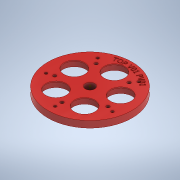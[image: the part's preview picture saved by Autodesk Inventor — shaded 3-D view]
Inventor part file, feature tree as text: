
AUTODESK INVENTOR PART (.ipt)
format: ipt  version: 2022.2 (Build 262287000, 287)  size: 698,880 bytes
history: native  units: in
note: dims shown in document units (in); Inventor stores cm internally (conversion verified against a paired STEP export)
features: sketch x8, extrude x5, hole x3, pattern_circular x1
ambient origin geometry x8: Origin, YZ Plane, XZ Plane, XY Plane, X Axis, Y Axis, Z Axis, Center Point
bodies: Body1 (feature_tree)
feature tree (17):
  extrude  "Extrusion5"  Depth=0.35in
  extrude  "TextForTop"  Depth=4.0in
  extrude  "Extrusion7"  Depth=0.04in TaperAngle=0.0deg
  pattern_circular  "Circular Pattern2"  Count=5  [1 undecoded]
  extrude  "Extrusion8"  Depth=0.51in
  sketch  "Sketch8"  dims[d30=0.3in d31=0.0in d32=1.9685in]
  extrude  "TextForBack"  Depth=0.2474in
  hole  "Hole2"  [1 undecoded]
  sketch  "Sketch13"  dims[d39=1.9685in d41=360.0deg d50=4.0in d51=0.05in d52=0.0in d54=3.0in d55=1.9685in d57=360.0deg d59=0.177in d60=0.75in d61=0.332in d62=0.25in d63=0.5635in d64=1.0in d65=0.8108in d67=0.3825in d68=1.9685in d70=360.0deg d72=0.15in d73=0.75in d74=0.5in d75=0.093in d76=0.5635in d77=1.0in d78=0.8108in d79=0.185in d80=0.75in d81=0.218in d82=0.2186in d83=0.5635in d84=0.2785in d85=0.0in]
  hole  "Hole3"  [1 undecoded]
  hole  "Hole4"  [1 undecoded]
  sketch  "Sketch1"  dims[d5=360.0deg d23=0.35in]
  sketch  "Sketch5"  dims[d24=0.0in d25=4.0in]
  sketch  "Sketch6"  dims[d26=45.0deg d27=0.04in d28=0.0in]
  sketch  "Sketch7"  dims[d29=1.23in]
  sketch  "Sketch10"  dims[d33=360.0deg d35=0.51in]
  sketch  "Sketch12"  dims[d36=0.0in d37=0.0in d38=0.2474in]
note: 4 required parameter values undecoded (feature->parameter linkage not recoverable at this tier; creation-order binding heuristic only, values carry confidence <= 0.55)
